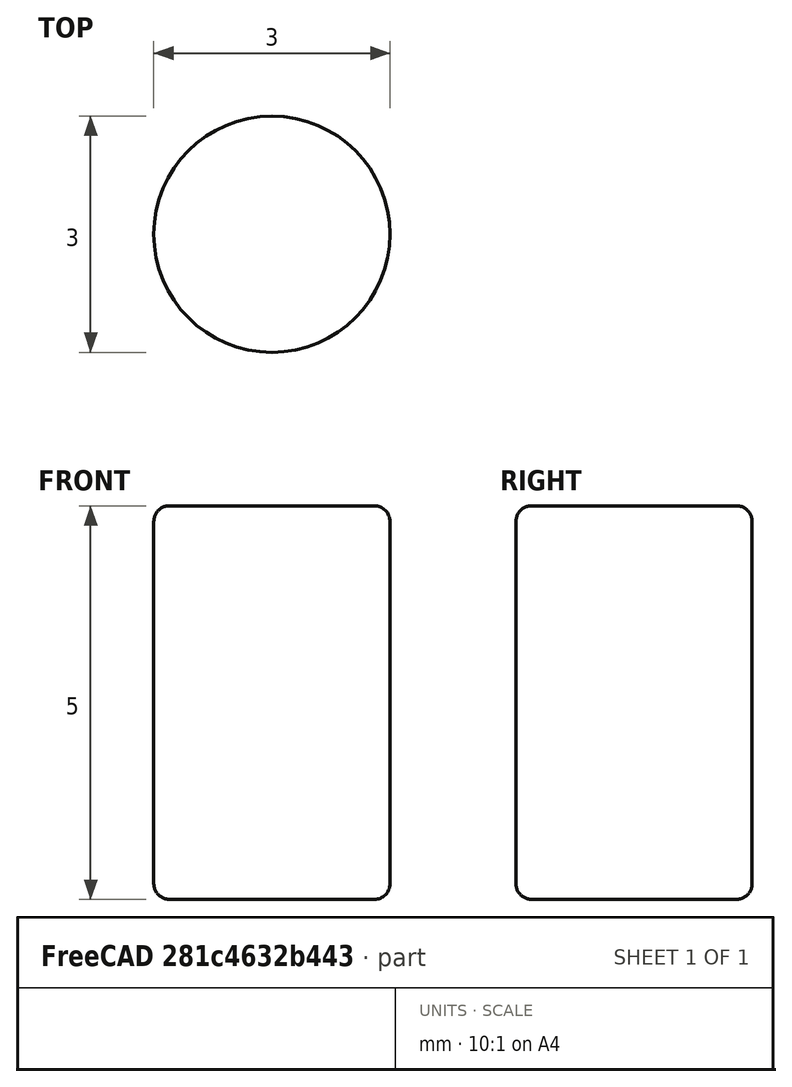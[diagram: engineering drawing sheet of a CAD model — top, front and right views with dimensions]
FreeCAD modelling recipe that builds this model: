
FCSTD DOCUMENT  (FreeCAD 1.1R41365 (Git))
Label: EncoderMagnet
License: All rights reserved
LicenseURL: https://en.wikipedia.org/wiki/All_rights_reserved
objects: App::Point×1, Sketcher::SketchObject×1, PartDesign::Pad×1, PartDesign::Fillet×1, PartDesign::Body×1
note: 9 computed .brp shape members not serialized (recipe doc carries the construction recipe); baked Part::Feature solids carry a one-line shape summary decoded from their .brp

FEATURE [App::Point] Origin001
  Role = Origin
FEATURE [Sketcher::SketchObject] Sketch
  ArcFitTolerance = 1e-06
  AttachmentSupport = -> [Origin]
  ExternalTypes = [0]
  FullyConstrained = true
  MakeInternals = false
  MapMode = 5
  sketch-geometry (1):
    g0: Circle CenterX=0 CenterY=0 CenterZ=0 NormalX=0 NormalY=0 NormalZ=1 AngleXU=0 Radius=1.5
  constraints (2):
    c: Coincident(g0,g-1)
    c: Diameter(g0) = 3
FEATURE [PartDesign::Pad] Pad
  Direction = (0,0,1)
  Length = 5
  Length2 = 10
  Midplane = true
  Profile = -> Sketch
  ReferenceAxis = -> Sketch [N_Axis]
  Refine = true
  Suppressed = false
  Type = 0
FEATURE [PartDesign::Fillet] Fillet
  Base = -> Pad [Edge3,Edge2]
  BaseFeature = -> Pad
  Radius = 0.2
  Refine = true
  SupportTransform = false
  Suppressed = false
  UseAllEdges = false
FEATURE [PartDesign::Body] Body  label="EncoderMagnet"
  AllowCompound = false
  Group = -> [Sketch,Pad,Fillet]
  Origin = -> Origin
  Tip = -> Fillet
